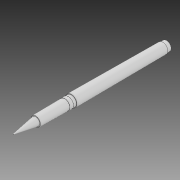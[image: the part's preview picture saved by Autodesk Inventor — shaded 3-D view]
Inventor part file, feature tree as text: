
AUTODESK INVENTOR PART (.ipt)
format: ipt  version: 2020 (Build 240168000, 168)  size: 114,176 bytes
history: native  units: mm
features: revolve x1, sketch x1
ambient origin geometry x8: Origin, YZ Plane, XZ Plane, XY Plane, X Axis, Y Axis, Z Axis, Center Point
bodies: Solid1 (feature_tree)
feature tree (2):
  revolve  "Revolution1"  [1 undecoded]
  sketch  "Sketch1"  dims[d0=3.875mm d1=3.2mm d2=4.25mm d3=4.8mm d4=80.3mm d5=4.325mm d6=2.5mm d7=3.0mm d8=4.4mm d9=4.25mm d10=4.0mm d11=3.375mm d12=129.1mm d13=30.0mm d14=90.0deg d15=0.2mm]
note: 1 required parameter value undecoded (feature->parameter linkage not recoverable at this tier; creation-order binding heuristic only, values carry confidence <= 0.55)
